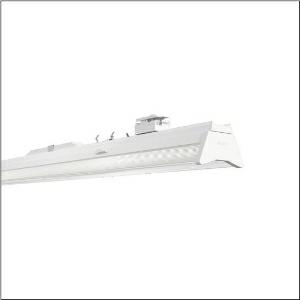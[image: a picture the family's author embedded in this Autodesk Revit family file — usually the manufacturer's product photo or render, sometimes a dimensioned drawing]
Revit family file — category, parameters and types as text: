
# Revit family: licross_11_performance_mo_51tm16dn35xg
name_source: partatom
category: Lighting Fixtures
units: mm (PartAtom-declared; Revit-internal decimal feet)

## family parameters
Cut with Voids When Loaded = No
Host = Face
Light Source = No
Part Type = Normal
Room Calculation Point = No
Round Connector Dimension = Use Diameter
Shared = No

## types (1)
- --- (1 x LED, 5100 lm, 28.3 W, 3000K)
    Apparent Load = 28 VA
    CIE Flux Codes = 66 88 96 79 100
    Color Rendering = 80
    Color Temperature = 3000K
    Default Elevation = 1800 mm
    Description = Licross 11 Performance MO, luminaire insert, of sheet steel, galvanised, coil coated, white, length: 1.500mm, width: 120mm, height: 123mm, LED rated luminous flux: 5.100lm, light colour: 830, SDCM (Standard Deviation of Colour Matching)MacAdam ≤ 2 SDCM (initial), control gear: DALI 2, with plug, 5-pole, with phase selection, mains connection: 220..240V, AC, 50/60Hz, rated input power: 28.3W, internal wiring halogen-free, primary light control with lens, of plastic, primary optical cover: cover, of PMMA, light emission: direct/indirect distribution, primary light characteristic: symmetric, protection rating (complete): IP40, insulation class (complete): insulation class I (protective earthing), certification: CE, ENEC, VDE, UKCA, protection symbol: D if used in an environment without relevant dust loads with corresponding accessories, impact resistance: IK06, permissible ambient temperature for indoor applications: -25..+45°C, corresponds to IFS (International Featured Standards) requirements for safety and quality in the food industry, reducing of maximum allowable ambient temperature of 5°C with ceiling mounting, LABS conformity tested according to VDMA 24364:2018-05, The light source and the operating device comply with the requirements of the Ecodesign Regulation (EU) 2019/2020 and are replaceable in accordance with this regulation, packaging unit: 1 piece
    Height = 114 mm
    Lamp = 1 x LED
    Lamp Light Flux = 5100 lm
    Lamp Power = 28.3 W
    Lamp count = 1
    Length = 1500 mm
    Luminous efficacy = 180 lm/W
    Manufacturer = Siteco
    ModVariant = No
    Model = 51TM16DN35XG
    Mounting Place = Ceiling
    Mounting Type = Pendant
    Number of Poles = 1
    OnlyDefault = Yes
    Power Factor = 1
    Product Name = Licross 11 Performance MO
    Product group = luminaire insert | ceiling pendant
    ProductGroupID = 901
    Protection Class = Protection class I
    Protection Degree = IP 40
    RLX_Detail_Level = 1
    RLX_Emergency_Light_Flux = 0 lm
    RLX_Emergency_Type = 0
    RLX_Emergency_Type_DB = No
    RlxData = <blob elided: 34133 chars, md5=316e854e>
    Socket = socket
    Standby Power = 0 W
    System Light Flux = 5100 lm
    System Power = 28 W
    Type Comments = factory setting: luminous flux: 100 % | dim-lin: 254 | 190 mA
    Type Image = l_1256138.jpg
    URL = http://relux.com
    VarID = @adj_075739
    Voltage = 0 V
    Weight = 0.00 kg
    Width = 120 mm

## geometry (parser evidence)
native form markers: Blend x4, Sweep x13
no freeform markers — native parametric forms only
